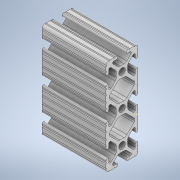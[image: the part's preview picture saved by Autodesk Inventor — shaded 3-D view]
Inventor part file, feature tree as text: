
AUTODESK INVENTOR PART (.ipt)
format: ipt  version: 2020 (Build 240168000, 168)  size: 366,080 bytes
history: native  units: in
note: dims shown in document units (in); Inventor stores cm internally (conversion verified against a paired STEP export)
features: sketch x2, extrude x1
ambient origin geometry x8: Origin, YZ Plane, XZ Plane, XY Plane, X Axis, Y Axis, Z Axis, Center Point
bodies: Solid1 (feature_tree)
feature tree (3):
  extrude  "Extrusion1"  [1 undecoded]
  sketch  "Sketch2"
  sketch  "Sketch1"  dims[d0=2.0in d1=0.0in]
note: 1 required parameter value undecoded (feature->parameter linkage not recoverable at this tier; creation-order binding heuristic only, values carry confidence <= 0.55)
